# Revit family: Building-IEC309Connections-GEWISS-66IB-INTERLOCKED-SOCKET-OUTLETS-HD_IP66_WITH_BOTTOM_FUS
name_source: partatom
category: Apparecchi elettrici
units: mm (PartAtom-declared; Revit-internal decimal feet)

## family parameters
Condiviso = Sì
Host = Superficie
Mantenere orientamento annotazione = Sì
Punto di calcolo locali = Sì
Quota connettore circolare = Usa diametro
Taglio con vuoti quando caricato = Sì
Tipo di parte = Normale

## types (1)
- Building-IEC309Connections-GEWISS-66IB-INTERLOCKED-SOCKET-OUTLETS-HD_IP66_WITH_BOTTOM_FUS
    Catalogue = BUILDING
    Catalogue Range = 66 IB
    Colour = Red
    Colour: = Red
    Corpo presa = Light Blue
    Descrizione = I.SOCKET IP66 W.B.3P+E 32A 380V 3H CBF
    EAN code = 8011564074446
    Electrocod = 2222
    Frequency = 50/60 Hz
    Glow Wire Test = 850 °C
    Glow wire test: = 850 °C
    IDF = 521e3e45-4fc9-41b1-a2a9-ba7bf81b8660
    IDT = 59f79668-9a62-484f-b845-13f84bd98f98
    IP degree = IP66
    Immagine tipo = S.jpg
    Impact resistance at -20 °C = 20J
    Modello = GW66973
    N_poli = 1
    No. of poles = 3P+E
    Number of poles = 3P+E
    Operating temperature: = -25 +40 °C
    Produttore = GEWISS S.p.A.
    Prospetto di default = 1219 mm
    Protection = Fuse-holder base (CBF)
    Rated current (A) = 32
    Rated current (In) = 32
    Rated frequency (Hz) = 50/60 Hz
    Rated voltage = 380-440V
    Reference h = 3
    SEO = Socket outlet
    Shock resistance = > IK10
    Simbolo presa = PRESAINDSTAGNA : 3P
    Struttura = Grigio RAL - 7035
    Technical sheet = https://www.gewiss.com
    Thermo-pressure with ball = 80
    Type of fuse = Ø 10.3x38 mm
    Type of use = Heavy duty
    Typology = Vertical
    URL = https://www.gewiss.com
    Version file RFA = 21.4
    With back-mounting box = Yes
    Working temperature = -25 ÷ +40 °C
    giallo = 0 mm  [stored 0 ft]
    presa = Grigio RAL - 7035
    vetro = Default - Vetro
    voltaggio = 0 V

note: source unit labels omitted for Thermo-pressure with ball — the stored unit's dimension contradicts the parameter name (converter mislabeling)

note: [stored X ft] marks values corroborated as IEEE doubles in the binary element streams (Revit-internal decimal feet)

## geometry (parser evidence)
native form markers: Sweep x6
no freeform markers — native parametric forms only
